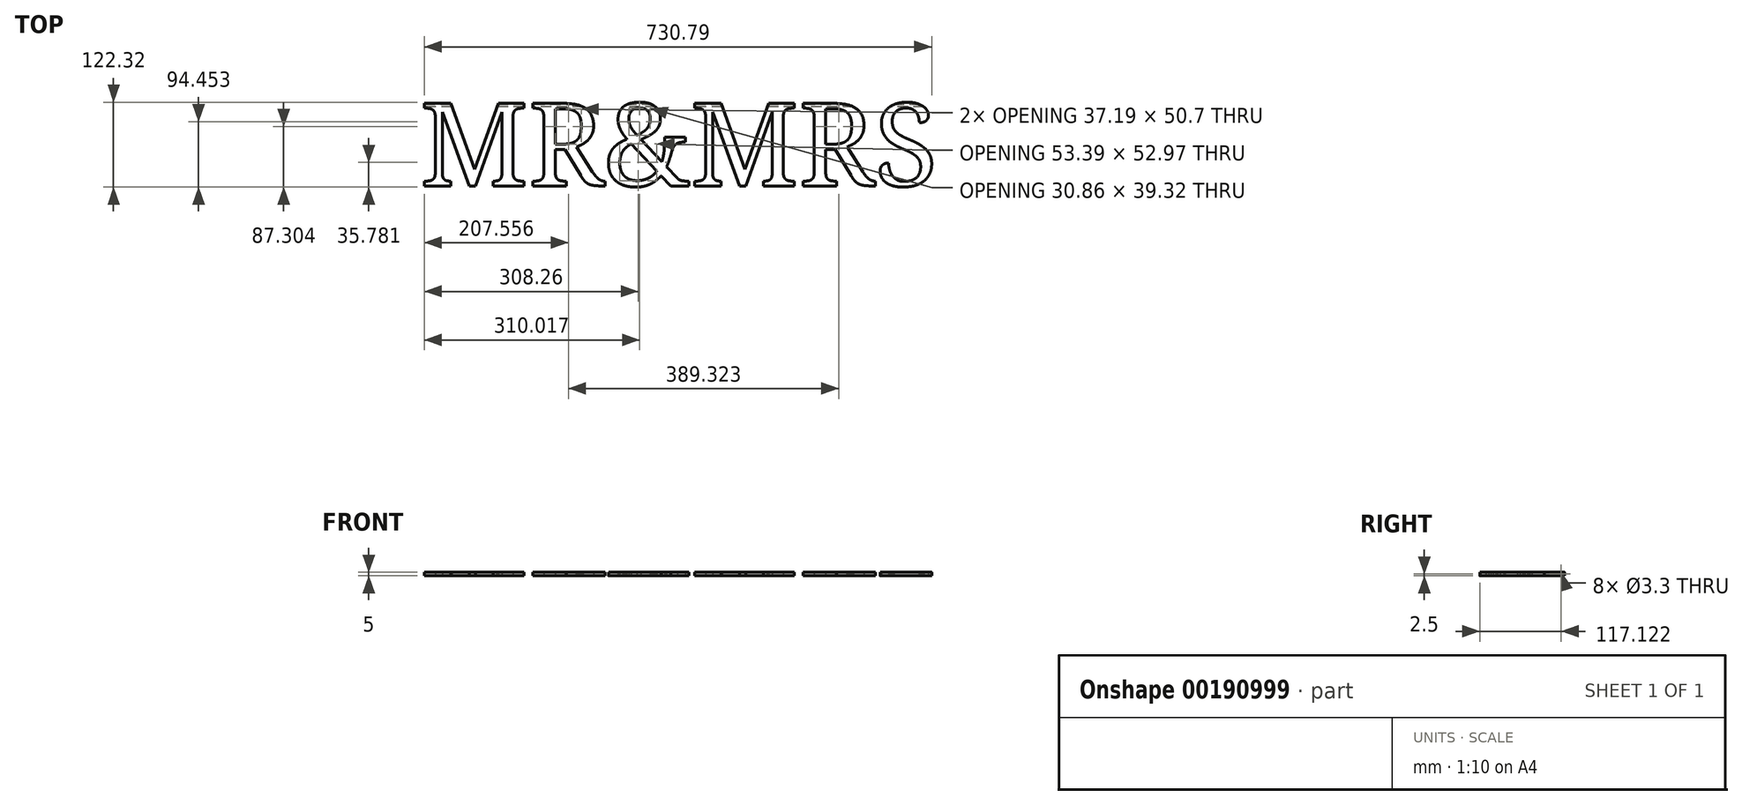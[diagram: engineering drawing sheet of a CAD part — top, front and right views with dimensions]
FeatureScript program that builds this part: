
annotation { "Feature Type Name" : "Feature", "Feature Type Description" : "" }
export const myFeature = defineFeature(function(context is Context, id is Id, definition is map)
    precondition{}
    {
        {
            var Q0;
            Q0=qCreatedBy(makeId("Top.planeOp"),FACE);
            var sketch = newSketch(context, id + "F0", { "sketchPlane" : qUnion([Q0])});
            skText(sketch, "E0", { "text": "MR&MRS", "fontName": "NotoSerif-Regular.ttf"});
            const initialGuessF0  = {"E0": [0, 0, 1, 0, 0.12]};
            skSetInitialGuess(sketch, initialGuessF0);
            skSolve(sketch);
        }
        {
            var Q0;
            Q0 = qSketchRegion(id + "F0", true);
            extrude(context, id + "F1", {"entities" : qUnion([Q0]), "depth" : 5 * mm});
        }
        {
            var Q0;
            Q0=makeQuery(id+"F1.opExtrude","SWEPT_FACE",FACE,{"disambiguationData":[OSD([sQuery(id+"F0.wireOp",EDGE,"E0.sketch_text.stroke-30")])]});
            var sketch = newSketch(context, id + "F2", { "sketchPlane" : qUnion([Q0])});
            skCircle(sketch, "E1", {"center": v(-115.48, 2.5) * mm, "radius": 1.65 * mm});
            skPoint(sketch, "E1.centerSnap0", {"position": v(-118.98, 2.5) * mm});
            skPoint(sketch, "E1.centerSnap1", {"position": v(-115.48, 0) * mm});
            skSolve(sketch);
        }
        {
            var Q0;
            Q0 = qSketchRegion(id + "F2", true);
            var Q1;
            Q1=makeQuery(id+"F1.opExtrude","SWEPT_BODY",BODY,{"disambiguationData":[OSD([sQuery(id+"F0.wireOp",EDGE,"E0.sketch_text.stroke-279"),sQuery(id+"F0.wireOp",EDGE,"E0.sketch_text.stroke-280"),sQuery(id+"F0.wireOp",EDGE,"E0.sketch_text.stroke-281"),sQuery(id+"F0.wireOp",EDGE,"E0.sketch_text.stroke-282"),sQuery(id+"F0.wireOp",EDGE,"E0.sketch_text.stroke-283"),sQuery(id+"F0.wireOp",EDGE,"E0.sketch_text.stroke-284"),sQuery(id+"F0.wireOp",EDGE,"E0.sketch_text.stroke-285"),sQuery(id+"F0.wireOp",EDGE,"E0.sketch_text.stroke-286"),sQuery(id+"F0.wireOp",EDGE,"E0.sketch_text.stroke-287"),sQuery(id+"F0.wireOp",EDGE,"E0.sketch_text.stroke-288"),sQuery(id+"F0.wireOp",EDGE,"E0.sketch_text.stroke-289"),sQuery(id+"F0.wireOp",EDGE,"E0.sketch_text.stroke-290"),sQuery(id+"F0.wireOp",EDGE,"E0.sketch_text.stroke-291"),sQuery(id+"F0.wireOp",EDGE,"E0.sketch_text.stroke-292"),sQuery(id+"F0.wireOp",EDGE,"E0.sketch_text.stroke-293"),sQuery(id+"F0.wireOp",EDGE,"E0.sketch_text.stroke-294"),sQuery(id+"F0.wireOp",EDGE,"E0.sketch_text.stroke-295"),sQuery(id+"F0.wireOp",EDGE,"E0.sketch_text.stroke-296"),sQuery(id+"F0.wireOp",EDGE,"E0.sketch_text.stroke-297"),sQuery(id+"F0.wireOp",EDGE,"E0.sketch_text.stroke-298"),sQuery(id+"F0.wireOp",EDGE,"E0.sketch_text.stroke-299"),sQuery(id+"F0.wireOp",EDGE,"E0.sketch_text.stroke-300"),sQuery(id+"F0.wireOp",EDGE,"E0.sketch_text.stroke-301"),sQuery(id+"F0.wireOp",EDGE,"E0.sketch_text.stroke-302"),sQuery(id+"F0.wireOp",EDGE,"E0.sketch_text.stroke-303"),sQuery(id+"F0.wireOp",EDGE,"E0.sketch_text.stroke-304"),sQuery(id+"F0.wireOp",EDGE,"E0.sketch_text.stroke-305"),sQuery(id+"F0.wireOp",EDGE,"E0.sketch_text.stroke-306"),sQuery(id+"F0.wireOp",EDGE,"E0.sketch_text.stroke-307"),sQuery(id+"F0.wireOp",EDGE,"E0.sketch_text.stroke-308"),sQuery(id+"F0.wireOp",EDGE,"E0.sketch_text.stroke-309"),sQuery(id+"F0.wireOp",EDGE,"E0.sketch_text.stroke-310"),sQuery(id+"F0.wireOp",EDGE,"E0.sketch_text.stroke-311"),sQuery(id+"F0.wireOp",EDGE,"E0.sketch_text.stroke-312"),sQuery(id+"F0.wireOp",EDGE,"E0.sketch_text.stroke-313"),sQuery(id+"F0.wireOp",EDGE,"E0.sketch_text.stroke-314"),sQuery(id+"F0.wireOp",EDGE,"E0.sketch_text.stroke-315"),sQuery(id+"F0.wireOp",EDGE,"E0.sketch_text.stroke-316"),sQuery(id+"F0.wireOp",EDGE,"E0.sketch_text.stroke-317"),sQuery(id+"F0.wireOp",EDGE,"E0.sketch_text.stroke-318"),sQuery(id+"F0.wireOp",EDGE,"E0.sketch_text.stroke-319"),sQuery(id+"F0.wireOp",EDGE,"E0.sketch_text.stroke-320"),sQuery(id+"F0.wireOp",EDGE,"E0.sketch_text.stroke-321"),sQuery(id+"F0.wireOp",EDGE,"E0.sketch_text.stroke-322"),sQuery(id+"F0.wireOp",EDGE,"E0.sketch_text.stroke-323"),sQuery(id+"F0.wireOp",EDGE,"E0.sketch_text.stroke-324"),sQuery(id+"F0.wireOp",EDGE,"E0.sketch_text.stroke-325"),sQuery(id+"F0.wireOp",EDGE,"E0.sketch_text.stroke-326"),sQuery(id+"F0.wireOp",EDGE,"E0.sketch_text.stroke-327"),sQuery(id+"F0.wireOp",EDGE,"E0.sketch_text.stroke-328")])]});
            extrude(context, id + "F3", {"entities" : qUnion([Q0]), "operationType" : NewBodyOperationType.REMOVE, "endBound" : BoundingType.THROUGH_ALL, "oppositeDirection" : true, "endBoundEntityBody" : qUnion([Q1]), "depth" : 25 * mm});
        }
        {
            var Q0;
            Q0=makeQuery(id+"F1.opExtrude","SWEPT_FACE",FACE,{"disambiguationData":[OSD([sQuery(id+"F0.wireOp",EDGE,"E0.sketch_text.stroke-80")])]});
            var sketch = newSketch(context, id + "F4", { "sketchPlane" : qUnion([Q0])});
            skCircle(sketch, "E2", {"center": v(-115.48, 2.5) * mm, "radius": 1.65 * mm});
            skSolve(sketch);
        }
        {
            var Q0;
            Q0 = qSketchRegion(id + "F4", true);
            extrude(context, id + "F5", {"entities" : qUnion([Q0]), "operationType" : NewBodyOperationType.REMOVE, "endBound" : BoundingType.THROUGH_ALL, "oppositeDirection" : true, "depth" : 25 * mm});
        }
        {
            var Q0;
            Q0=qCreatedBy(makeId("Right.planeOp"),FACE);
            var sketch = newSketch(context, id + "F6", { "sketchPlane" : qUnion([Q0])});
            skCircle(sketch, "E3", {"center": v(115.48, 2.5) * mm, "radius": 1.65 * mm});
            skSolve(sketch);
        }
        {
            var Q0;
            Q0 = qSketchRegion(id + "F6", true);
            extrude(context, id + "F7", {"entities" : qUnion([Q0]), "operationType" : NewBodyOperationType.REMOVE, "endBound" : BoundingType.THROUGH_ALL, "depth" : 25 * mm});
        }
    });
